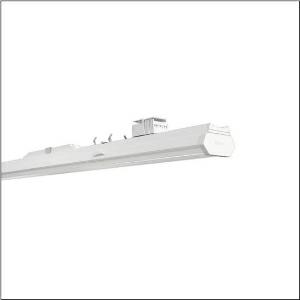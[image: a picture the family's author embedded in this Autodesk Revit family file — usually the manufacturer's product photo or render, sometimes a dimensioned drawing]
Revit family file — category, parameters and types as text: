
# Revit family: licross_r__11_protected_mo_51td12vn455f_ccae
name_source: partatom
category: Lighting Fixtures
units: mm (PartAtom-declared; Revit-internal decimal feet)

## family parameters
Cut with Voids When Loaded = No
Host = Face
Light Source = No
Part Type = Normal
Room Calculation Point = No
Round Connector Dimension = Use Diameter
Shared = No

## types (1)
- --- (1 x LED, 5500 lm, 33.9 W, 4000K)
    Apparent Load = 34 VA
    CIE Flux Codes = 73 92 98 99 100
    Color Rendering = 80
    Color Temperature = 4000K
    Default Elevation = 1800 mm
    Description = Licross® 11 Protected MO, luminaire insert, of sheet steel, galvanised, coil coated, white, length: 1.500mm, width: 90mm, height: 101mm, LED rated luminous flux: 5.500lm, light colour: 840, control gear: DALI 2, CLO, control gear: ECG DALI, with plug, 5-pole, with phase selection, mains connection: 220..240V, AC, 50/60Hz, halogen-free wiring, primary optical cover: cover, of PMMA, light emission: direct with ceiling illumination distribution, protection rating (complete): IP54, insulation class (complete): insulation class I (protective earthing), certification: CE, ENEC, VDE, UKCA, protection symbol: D if used in an environment with non-conductive dust loads with corresponding accessories, permissible ambient temperature for indoor applications: -25..+45°C, corresponds to IFS (International Featured Standards) requirements for safety and quality in the food industry, reducing of maximum allowable ambient temperature of 5°C with ceiling mounting, LABS conformity tested according to VDMA 24364:2018-05, packaging unit: 1 piece
    Height = 92 mm
    Lamp = 1 x LED
    Lamp Light Flux = 5500 lm
    Lamp Power = 33.9 W
    Lamp count = 1
    Length = 1500 mm
    Luminous efficacy = 162 lm/W
    Manufacturer = Siteco
    ModVariant = No
    Model = 51TD12VN455F
    Mounting Place = Ceiling
    Mounting Type = Pendant
    Number of Poles = 1
    OnlyDefault = Yes
    Power Factor = 1
    Product Name = Licross® 11 Protected MO
    Product group = luminaire insert
    ProductGroupID = 902
    Protection Class = Protection class I
    Protection Degree = IP 54
    RLX_Detail_Level = 1
    RlxData = <blob elided: 24373 chars, md5=8041bba8>
    Socket = socket
    Standby Power = 0 W
    System Light Flux = 5500 lm
    System Power = 34 W
    Type Comments = factory setting: luminous flux: 100 % | dim-lin: 254 | 222 mA
    Type Image = l_1256145.jpg
    URL = http://relux.com
    VarID = @adj_060705
    Voltage = 0 V
    Weight = 0.00 kg
    Width = 88 mm

## geometry (parser evidence)
native form markers: Blend x4, Sweep x11
no freeform markers — native parametric forms only
